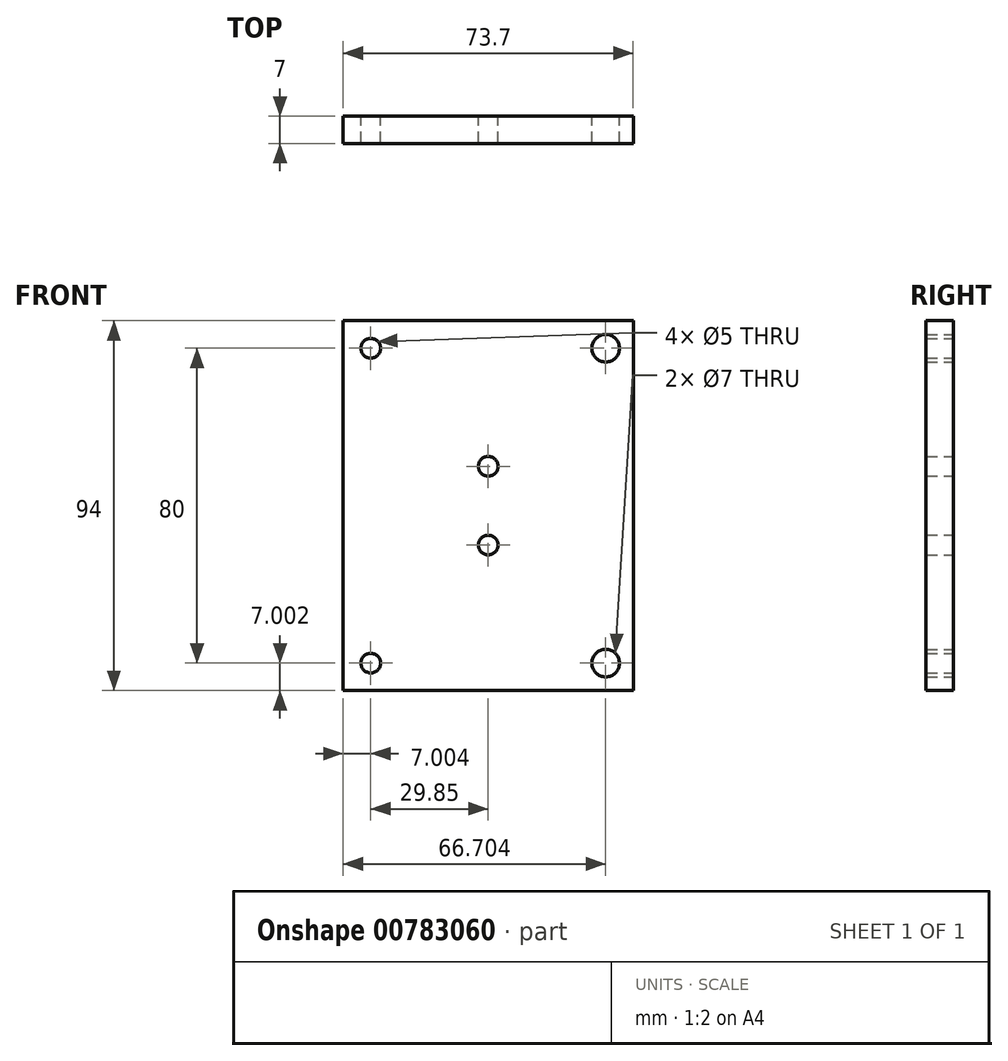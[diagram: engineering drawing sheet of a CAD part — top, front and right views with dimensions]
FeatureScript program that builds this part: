
annotation { "Feature Type Name" : "Feature", "Feature Type Description" : "" }
export const myFeature = defineFeature(function(context is Context, id is Id, definition is map)
    precondition{}
    {
        {
            var Q0;
            Q0=qCreatedBy(makeId("Front.planeOp"),FACE);
            var sketch = newSketch(context, id + "F0", { "sketchPlane" : qUnion([Q0])});
            skLineSegment(sketch, "E0.bottom", {"start": v(-43.97, 65.1) * mm, "end": v(29.73, 65.1) * mm});
            skLineSegment(sketch, "E0.top", {"start": v(-43.97, -28.9) * mm, "end": v(29.73, -28.9) * mm});
            skLineSegment(sketch, "E0.left", {"start": v(-43.97, 65.1) * mm, "end": v(-43.97, -28.9) * mm});
            skLineSegment(sketch, "E0.right", {"start": v(29.73, 65.1) * mm, "end": v(29.73, -28.9) * mm});
            skCircle(sketch, "E1", {"center": v(-36.97, -21.9) * mm, "radius": 2.5 * mm});
            skCircle(sketch, "E2", {"center": v(22.73, -21.9) * mm, "radius": 3.5 * mm});
            skCircle(sketch, "E3.0.1.0", {"center": v(-36.97, 58.1) * mm, "radius": 2.5 * mm});
            skCircle(sketch, "E3.0.1.1", {"center": v(22.73, 58.1) * mm, "radius": 3.5 * mm});
            skLineSegment(sketch, "E3.direction1", {"start": v(-36.97, -21.9) * mm, "end": v(-32.97, -21.9) * mm, "construction": true});
            skLineSegment(sketch, "E3.direction2", {"start": v(-36.97, -21.9) * mm, "end": v(-36.97, 58.1) * mm, "construction": true});
            skCircle(sketch, "E4", {"center": v(-7.12, 28.1) * mm, "radius": 2.5 * mm});
            skCircle(sketch, "E5", {"center": v(-7.12, 8.1) * mm, "radius": 2.5 * mm});
            skLineSegment(sketch, "E6", {"start": v(-7.12, 65.1) * mm, "end": v(-7.12, -28.9) * mm});
            skLineSegment(sketch, "E7", {"start": v(29.73, 18.1) * mm, "end": v(-43.97, 18.1) * mm});
            skSolve(sketch);
        }
        {
            var Q0;
            Q0 = qSketchRegion(id + "F0", true);
            extrude(context, id + "F1", {"entities" : qUnion([Q0]), "depth" : 7 * mm, "offsetDistance" : 25 * mm});
        }
    });
